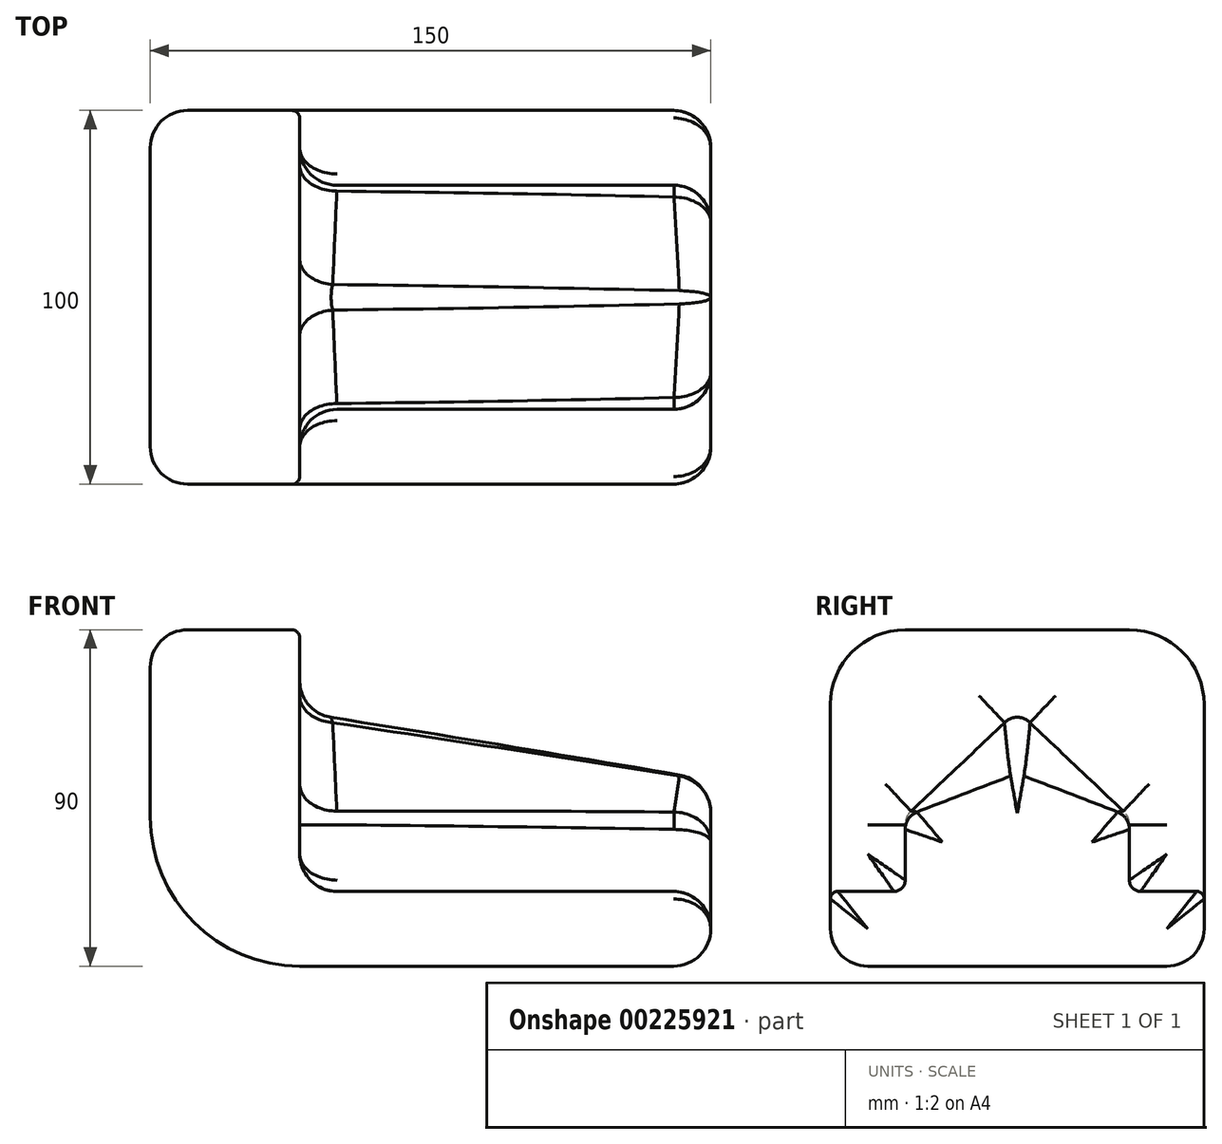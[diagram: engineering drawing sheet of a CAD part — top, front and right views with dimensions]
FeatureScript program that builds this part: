
annotation { "Feature Type Name" : "Feature", "Feature Type Description" : "" }
export const myFeature = defineFeature(function(context is Context, id is Id, definition is map)
    precondition{}
    {
        {
            var Q0;
            Q0=qCreatedBy(makeId("Top.planeOp"),FACE);
            var sketch = newSketch(context, id + "F0", { "sketchPlane" : qUnion([Q0])});
            skLineSegment(sketch, "E0.bottom", {"start": v(0, 50) * mm, "end": v(150, 50) * mm});
            skLineSegment(sketch, "E0.top", {"start": v(0, -50) * mm, "end": v(150, -50) * mm});
            skLineSegment(sketch, "E0.left", {"start": v(0, 50) * mm, "end": v(0, -50) * mm});
            skLineSegment(sketch, "E0.right", {"start": v(150, 50) * mm, "end": v(150, -50) * mm});
            skSolve(sketch);
        }
        {
            var Q0;
            Q0 = qSketchRegion(id + "F0", true);
            extrude(context, id + "F1", {"entities" : qUnion([Q0]), "depth" : 90 * mm});
        }
        {
            var Q0;
            Q0=makeQuery(id+"F1.opExtrude","SWEPT_FACE",FACE,{"disambiguationData":[OSD([sQuery(id+"F0.wireOp",EDGE,"E0.right")])]});
            var sketch = newSketch(context, id + "F2", { "sketchPlane" : qUnion([Q0])});
            skLineSegment(sketch, "E1", {"start": v(-60, 20) * mm, "end": v(-30, 20) * mm});
            skLineSegment(sketch, "E2", {"start": v(-30, 20) * mm, "end": v(-30, 40) * mm});
            skLineSegment(sketch, "E3", {"start": v(-30, 40) * mm, "end": v(0, 50) * mm});
            skLineSegment(sketch, "E4", {"start": v(0, 50) * mm, "end": v(30, 40) * mm});
            skLineSegment(sketch, "E5", {"start": v(30, 40) * mm, "end": v(30, 20) * mm});
            skLineSegment(sketch, "E6", {"start": v(30, 20) * mm, "end": v(60, 20) * mm});
            skLineSegment(sketch, "E7", {"start": v(60, 20) * mm, "end": v(60, 100) * mm});
            skLineSegment(sketch, "E8", {"start": v(60, 100) * mm, "end": v(-60, 100) * mm});
            skLineSegment(sketch, "E9", {"start": v(-60, 100) * mm, "end": v(-60, 20) * mm});
            skSolve(sketch);
        }
        {
            var Q0;
            Q0=qCreatedBy(makeId("Right.planeOp"),FACE);
            cPlane(context, id + "F3", {"entities" : qUnion([Q0]), "cplaneType" : CPlaneType.OFFSET, "offset" : 40 * mm, "width" : 150 * mm, "height" : 150 * mm});
        }
        {
            var Q0;
            Q0=qCreatedBy(id+"F3.planeOp",FACE);
            var sketch = newSketch(context, id + "F4", { "sketchPlane" : qUnion([Q0])});
            skLineSegment(sketch, "E10", {"start": v(-60, 20) * mm, "end": v(-30, 20) * mm});
            skLineSegment(sketch, "E11", {"start": v(-30, 20) * mm, "end": v(-30, 40) * mm});
            skLineSegment(sketch, "E12", {"start": v(-30, 40) * mm, "end": v(0, 70) * mm});
            skLineSegment(sketch, "E13", {"start": v(0, 70) * mm, "end": v(30, 40) * mm});
            skLineSegment(sketch, "E14", {"start": v(30, 40) * mm, "end": v(30, 20) * mm});
            skLineSegment(sketch, "E15", {"start": v(30, 20) * mm, "end": v(60, 20) * mm});
            skLineSegment(sketch, "E16", {"start": v(60, 20) * mm, "end": v(60, 100) * mm});
            skLineSegment(sketch, "E17", {"start": v(60, 100) * mm, "end": v(-60, 100) * mm});
            skLineSegment(sketch, "E18", {"start": v(-60, 100) * mm, "end": v(-60, 20) * mm});
            skSolve(sketch);
        }
        {
            var Q1;
            Q1=makeQuery(id+"F4.imprint","IMPRINT",FACE,{"disambiguationData":[TD([[makeQuery(id+"F4.imprint","IMPRINT",EDGE,{"derivedFrom":sQuery(id+"F4.wireOp",EDGE,"E10")}),1.0]])]});
            var Q2;
            {var subQ5=sQuery(id+"F2.wireOp",EDGE,"E2");Q2=makeQuery(id+"F2.imprint","IMPRINT",FACE,{"disambiguationData":[TD([[makeQuery(id+"F2.imprint","IMPRINT",EDGE,{"derivedFrom":subQ5}),1.0]])]});}
            loft(context, id + "F5", {"operationType" : NewBodyOperationType.REMOVE, "sheetProfilesArray" : [{ "sheetProfileEntities" : qUnion([Q1]) }, { "sheetProfileEntities" : qUnion([Q2]) }]});
        }
        {
            var Q0;
            Q0=makeQuery(id+"F1.opExtrude","CAP_EDGE",EDGE,{"disambiguationData":[OSD([sQuery(id+"F0.wireOp",EDGE,"E0.left")])],"isStart":true});
            fillet(context, id + "F6", {"entities" : qUnion([Q0]), "radius" : 40 * mm, "tangentPropagation" : true, "allowEdgeOverflow" : false});
        }
        {
            var Q0;
            Q0=makeQuery(id+"F1.opExtrude","CAP_EDGE",EDGE,{"disambiguationData":[OSD([sQuery(id+"F0.wireOp",EDGE,"E0.top")])],"isStart":false});
            var Q1;
            Q1=makeQuery(id+"F1.opExtrude","CAP_EDGE",EDGE,{"disambiguationData":[OSD([sQuery(id+"F0.wireOp",EDGE,"E0.bottom")])],"isStart":false});
            fillet(context, id + "F7", {"entities" : qUnion([Q0, Q1]), "radius" : 20 * mm, "tangentPropagation" : true, "allowEdgeOverflow" : false});
        }
        {
            var Q0;
            Q0=makeQuery(id+"F5.boolean.opBoolean","COPY",EDGE,{"derivedFrom":makeQuery(id+"F5.opLoft","SWEPT_EDGE",EDGE,{"disambiguationData":[OSD([sQuery(id+"F2.wireOp",EDGE,"E2"),sQuery(id+"F2.wireOp",EDGE,"E3"),sQuery(id+"F4.wireOp",EDGE,"E11"),sQuery(id+"F4.wireOp",EDGE,"E12")])]})});
            var Q1;
            Q1=makeQuery(id+"F5.boolean.opBoolean","COPY",EDGE,{"derivedFrom":makeQuery(id+"F5.opLoft","SWEPT_EDGE",EDGE,{"disambiguationData":[OSD([sQuery(id+"F2.wireOp",EDGE,"E3"),sQuery(id+"F2.wireOp",EDGE,"E4"),sQuery(id+"F4.wireOp",EDGE,"E12"),sQuery(id+"F4.wireOp",EDGE,"E13")])]})});
            var Q2;
            Q2=makeQuery(id+"F5.boolean.opBoolean","COPY",EDGE,{"derivedFrom":makeQuery(id+"F5.opLoft","SWEPT_EDGE",EDGE,{"disambiguationData":[OSD([sQuery(id+"F2.wireOp",EDGE,"E4"),sQuery(id+"F2.wireOp",EDGE,"E5"),sQuery(id+"F4.wireOp",EDGE,"E13"),sQuery(id+"F4.wireOp",EDGE,"E14")])]})});
            fillet(context, id + "F8", {"entities" : qUnion([Q0, Q1, Q2]), "radius" : 5 * mm, "tangentPropagation" : true, "allowEdgeOverflow" : false});
        }
        {
            var Q0;
            Q0=makeQuery(id+"F5.boolean.opBoolean","COPY",EDGE,{"derivedFrom":makeQuery(id+"F5.opLoft","SWEPT_EDGE",EDGE,{"disambiguationData":[OSD([sQuery(id+"F2.wireOp",EDGE,"E1"),sQuery(id+"F2.wireOp",EDGE,"E2"),sQuery(id+"F4.wireOp",EDGE,"E10"),sQuery(id+"F4.wireOp",EDGE,"E11")])]})});
            var Q1;
            Q1=makeQuery(id+"F5.boolean.opBoolean","COPY",EDGE,{"derivedFrom":makeQuery(id+"F5.opLoft","SWEPT_EDGE",EDGE,{"disambiguationData":[OSD([sQuery(id+"F2.wireOp",EDGE,"E5"),sQuery(id+"F2.wireOp",EDGE,"E6"),sQuery(id+"F4.wireOp",EDGE,"E14"),sQuery(id+"F4.wireOp",EDGE,"E15")])]})});
            fillet(context, id + "F9", {"entities" : qUnion([Q0, Q1]), "radius" : 3 * mm, "tangentPropagation" : true, "allowEdgeOverflow" : false});
        }
        {
            var Q0;
            Q0=makeQuery(id+"F5.boolean.opBoolean","COPY",EDGE,{"derivedFrom":makeQuery(id+"F5.opLoft","MID_CAP_EDGE",EDGE,{"disambiguationData":[OSD([sQuery(id+"F4.wireOp",EDGE,"E10"),sQuery(id+"F4.wireOp",EDGE,"E11"),sQuery(id+"F4.wireOp",EDGE,"E18")])],"capPos":0.0})});
            fillet(context, id + "F10", {"entities" : qUnion([Q0]), "radius" : 10 * mm, "tangentPropagation" : true, "allowEdgeOverflow" : false});
        }
        {
            var Q0;
            Q0=makeQuery(id+"F5.boolean.opBoolean","INTERSECT",EDGE,{"derivedFrom":[makeQuery(id+"F1.opExtrude","CAP_FACE",FACE,{"disambiguationData":[OSD([sQuery(id+"F0.wireOp",EDGE,"E0.bottom"),sQuery(id+"F0.wireOp",EDGE,"E0.top"),sQuery(id+"F0.wireOp",EDGE,"E0.left"),sQuery(id+"F0.wireOp",EDGE,"E0.right")])],"isStart":false}),makeQuery(id+"F5.opLoft","CAP_FACE",FACE,{"disambiguationData":[OSD([makeQuery(id+"F4.imprint","IMPRINT",FACE,{"disambiguationData":[TD([[makeQuery(id+"F4.imprint","IMPRINT",EDGE,{"derivedFrom":sQuery(id+"F4.wireOp",EDGE,"E10")}),1.0]])]})])],"isStart":true})]});
            fillet(context, id + "F11", {"entities" : qUnion([Q0]), "radius" : 2 * mm, "tangentPropagation" : true, "allowEdgeOverflow" : false});
        }
        {
            var Q0;
            Q0=makeQuery(id+"F1.opExtrude","SWEPT_EDGE",EDGE,{"disambiguationData":[OSD([sQuery(id+"F0.wireOp",EDGE,"E0.top"),sQuery(id+"F0.wireOp",EDGE,"E0.right")])]});
            fillet(context, id + "F12", {"entities" : qUnion([Q0]), "radius" : 10 * mm, "tangentPropagation" : true, "allowEdgeOverflow" : false});
        }
        {
            var Q0;
            Q0=makeQuery(id+"F1.opExtrude","CAP_EDGE",EDGE,{"disambiguationData":[OSD([sQuery(id+"F0.wireOp",EDGE,"E0.left")])],"isStart":false});
            fillet(context, id + "F13", {"entities" : qUnion([Q0]), "radius" : 10 * mm, "tangentPropagation" : true, "allowEdgeOverflow" : false});
        }
    });
